# Revit family: Storage-Mounted-Teknion-BCLL_Cubic-with_Solid_Doors-Low_Secondary-R2015
name_source: partatom
category: Furniture
revit_build: Autodesk Revit Architecture 2015 (Build: 20140323_1530(x64)
units: mm (PartAtom-declared; Revit-internal decimal feet)

## types (2) — shared parameters
Assembly Code = E2020200
Manufacturer = Teknion
Manufacturer Fax = 416.661.4586
Part Number = BCLL
Product Documentation Link = http://www.teknion.com
Product Line = Expansion Casegoods
Product Page URL = http://www.teknion.com
Series = Expansion Casegoods
Sustainability Data = http://www.teknion.com
URL = www.teknion.com
Unit Weight URL = http://www.teknion.com
Warranty = http://www.teknion.com

## per-type parameters (varying)
| type | Actual Height | Description | Height | Model |
| 18"d x 18"w x 66"h | 65.165 " | Cubic Tower w Solid Doors-Low Sec Desk Mount,18"d x 18"w x 66"h | 66 " | BCLL__181866 |
| 18"d x 18"w x 72"h | 71.406 " | Cubic Tower w Solid Doors-Low Sec Desk Mount,18"d x 18"w x 72"h | 72 " | BCLL__181872 |

## geometry (parser evidence)
native form markers: Blend x6, Sweep x2
no freeform markers — native parametric forms only
